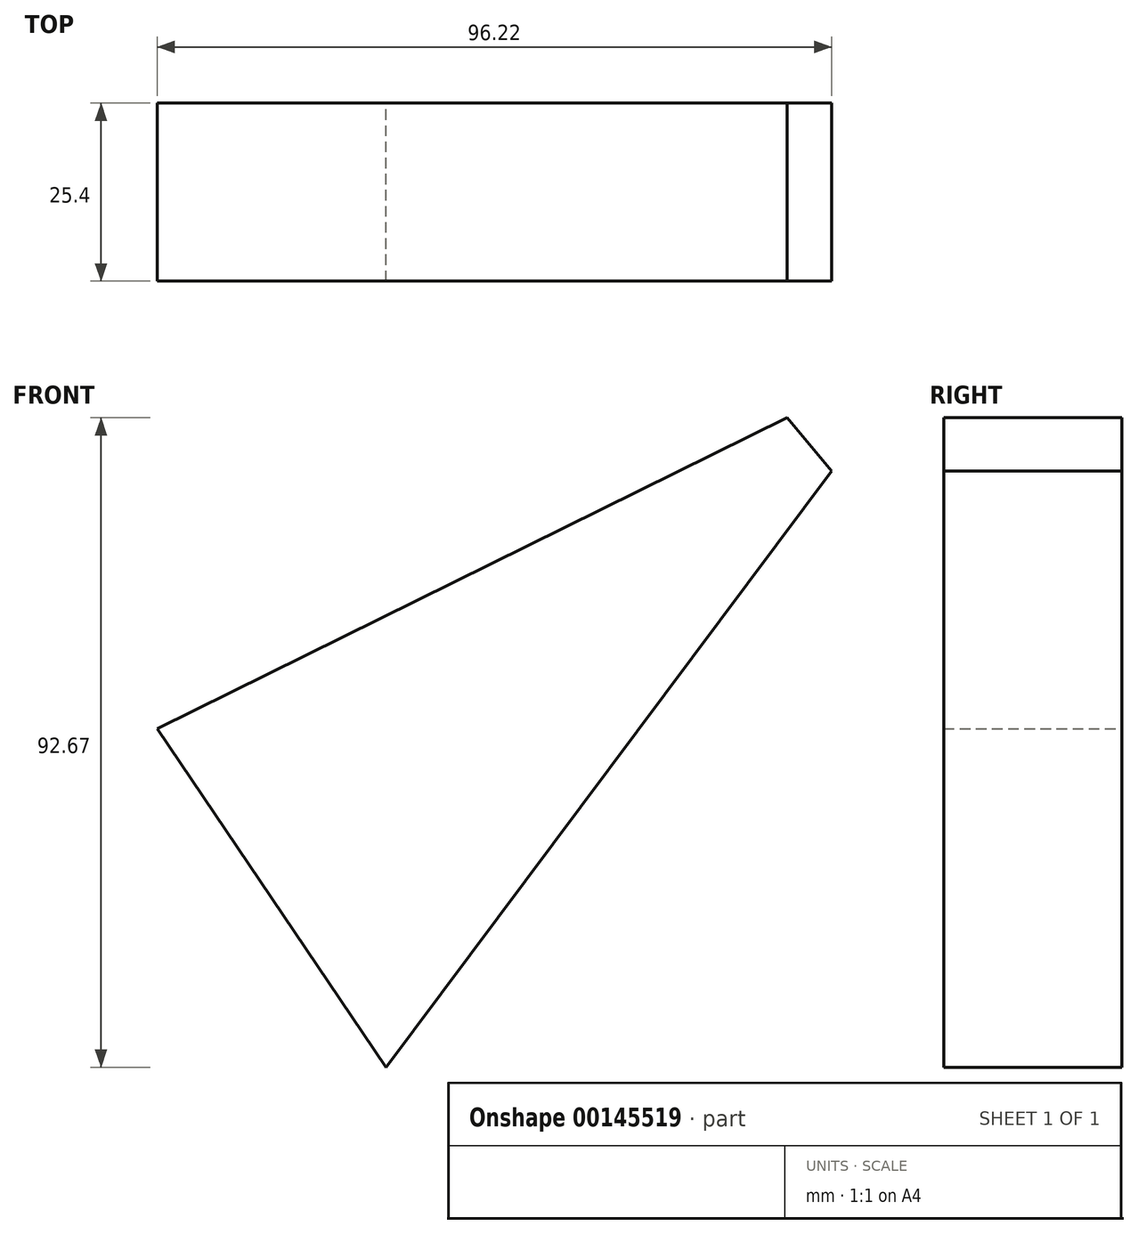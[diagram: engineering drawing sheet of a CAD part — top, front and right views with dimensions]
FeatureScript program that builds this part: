
annotation { "Feature Type Name" : "Feature", "Feature Type Description" : "" }
export const myFeature = defineFeature(function(context is Context, id is Id, definition is map)
    precondition{}
    {
        {
            var Q0;
            Q0=qCreatedBy(makeId("Front.planeOp"),FACE);
            var sketch = newSketch(context, id + "F0", { "sketchPlane" : qUnion([Q0])});
            skLineSegment(sketch, "E0", {"start": v(0, 0) * mm, "end": v(76.26, 102.05) * mm});
            skLineSegment(sketch, "E1", {"start": v(0, 0) * mm, "end": v(-32.64, 48.32) * mm});
            skLineSegment(sketch, "E2", {"start": v(-32.64, 48.32) * mm, "end": v(76.26, 102.05) * mm});
            skSolve(sketch);
        }
        {
            var Q0;
            Q0=makeQuery(id+"F0.imprint","IMPRINT",FACE,{"disambiguationData":[TD([[makeQuery(id+"F0.imprint","IMPRINT",EDGE,{"derivedFrom":sQuery(id+"F0.wireOp",EDGE,"E0")}),1.0]])]});
            extrude(context, id + "F1", {"entities" : qUnion([Q0]), "depth" : 25.4 * mm});
        }
        {
            var Q0;
            Q0=makeQuery(id+"F1.opExtrude","SWEPT_EDGE",EDGE,{"disambiguationData":[OSD([sQuery(id+"F0.wireOp",EDGE,"E0"),sQuery(id+"F0.wireOp",EDGE,"E2")])]});
            chamfer(context, id + "F2", {"entities" : qUnion([Q0]), "width" : 5.08 * mm, "tangentPropagation" : true});
        }
    });
